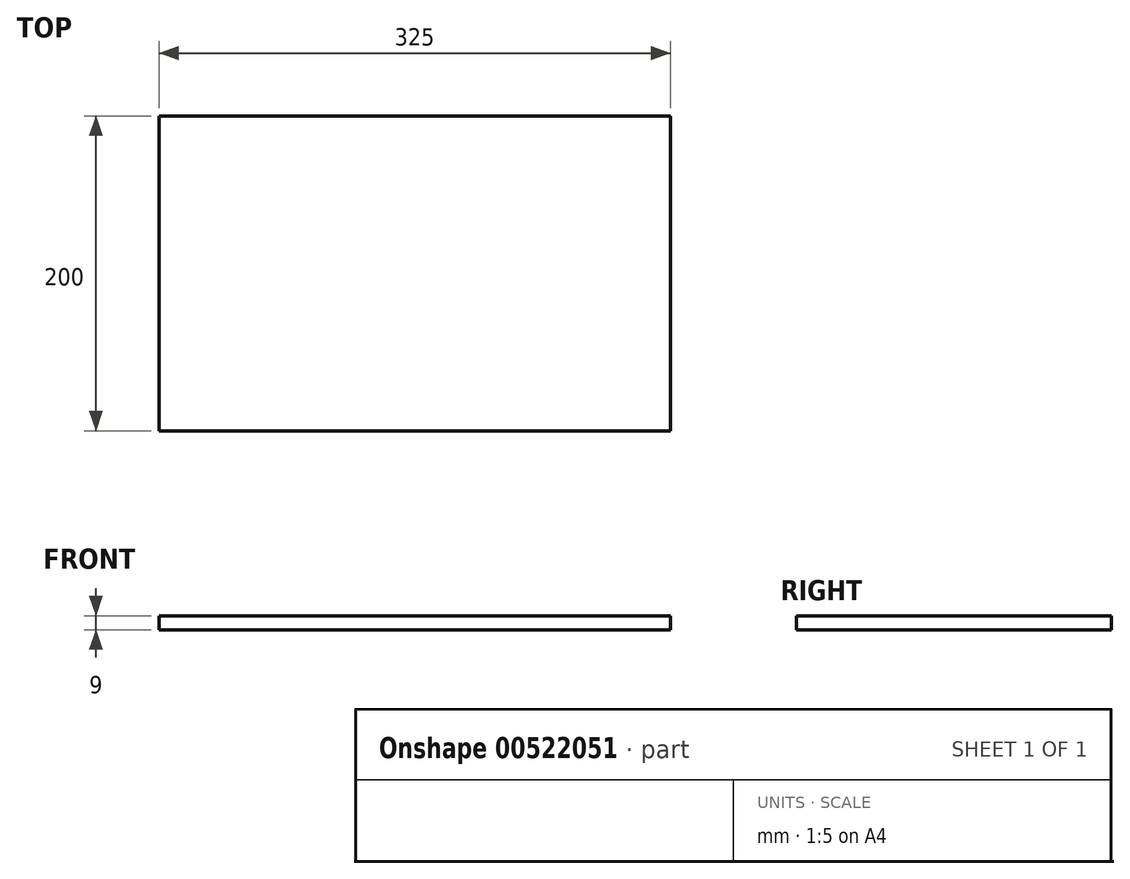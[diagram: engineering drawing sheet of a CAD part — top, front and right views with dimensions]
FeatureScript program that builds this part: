
annotation { "Feature Type Name" : "Feature", "Feature Type Description" : "" }
export const myFeature = defineFeature(function(context is Context, id is Id, definition is map)
    precondition{}
    {
        {
            var Q0;
            Q0=qCreatedBy(makeId("Top.planeOp"),FACE);
            var sketch = newSketch(context, id + "F0", { "sketchPlane" : qUnion([Q0])});
            skLineSegment(sketch, "E0.bottom", {"start": v(0, 0) * mm, "end": v(-325, 0) * mm});
            skLineSegment(sketch, "E0.top", {"start": v(0, 200) * mm, "end": v(-325, 200) * mm});
            skLineSegment(sketch, "E0.left", {"start": v(0, 0) * mm, "end": v(0, 200) * mm});
            skLineSegment(sketch, "E0.right", {"start": v(-325, 0) * mm, "end": v(-325, 200) * mm});
            skSolve(sketch);
        }
        {
            var Q0;
            Q0=makeQuery(id+"F0.imprint","IMPRINT",FACE,{"disambiguationData":[TD([[makeQuery(id+"F0.imprint","IMPRINT",EDGE,{"derivedFrom":sQuery(id+"F0.wireOp",EDGE,"E0.bottom")}),-1.0]])]});
            extrude(context, id + "F1", {"entities" : qUnion([Q0]), "depth" : 9 * mm, "offsetDistance" : 25 * mm});
        }
    });
